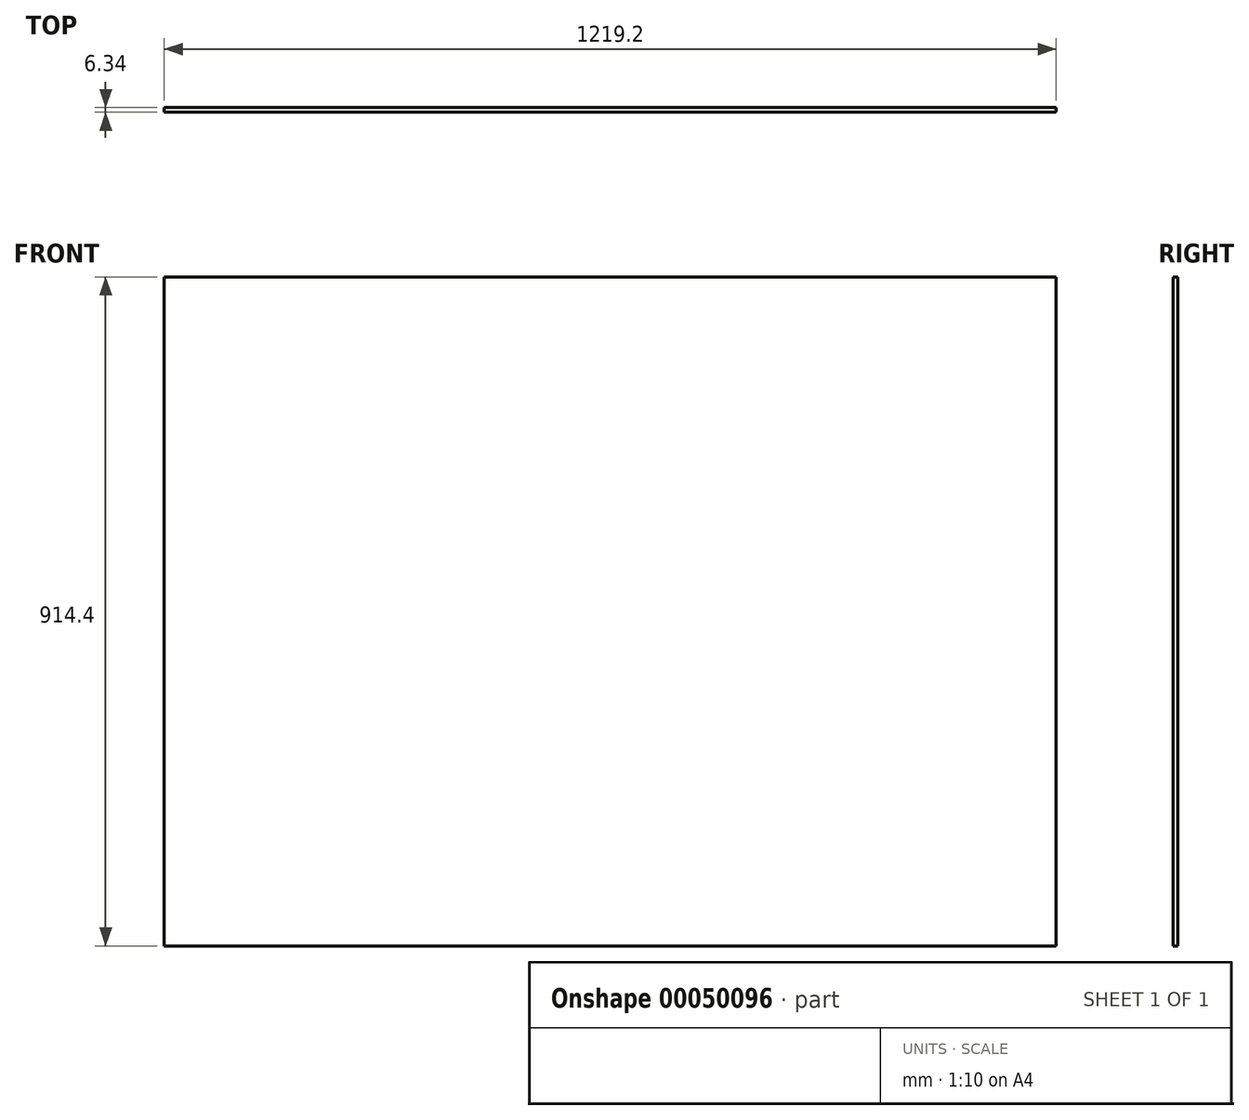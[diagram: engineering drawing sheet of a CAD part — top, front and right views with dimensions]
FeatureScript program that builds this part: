
annotation { "Feature Type Name" : "Feature", "Feature Type Description" : "" }
export const myFeature = defineFeature(function(context is Context, id is Id, definition is map)
    precondition{}
    {
        {
            var Q0;
            Q0=qCreatedBy(makeId("Top.planeOp"),FACE);
            var sketch = newSketch(context, id + "F0", { "sketchPlane" : qUnion([Q0])});
            skLineSegment(sketch, "E0.top", {"start": v(-609.6, -3.18) * mm, "end": v(609.6, -3.18) * mm});
            skLineSegment(sketch, "E0.left", {"start": v(-609.6, 3.18) * mm, "end": v(-609.6, -3.18) * mm});
            skLineSegment(sketch, "E0.right", {"start": v(609.6, 3.18) * mm, "end": v(609.6, -3.18) * mm});
            skLineSegment(sketch, "E1", {"start": v(-609.6, 3.18) * mm, "end": v(609.6, 3.18) * mm});
            skSolve(sketch);
        }
        {
            var Q0;
            Q0 = qSketchRegion(id + "F0", true);
            extrude(context, id + "F1", {"entities" : qUnion([Q0]), "depth" : 914.4 * mm});
        }
    });
